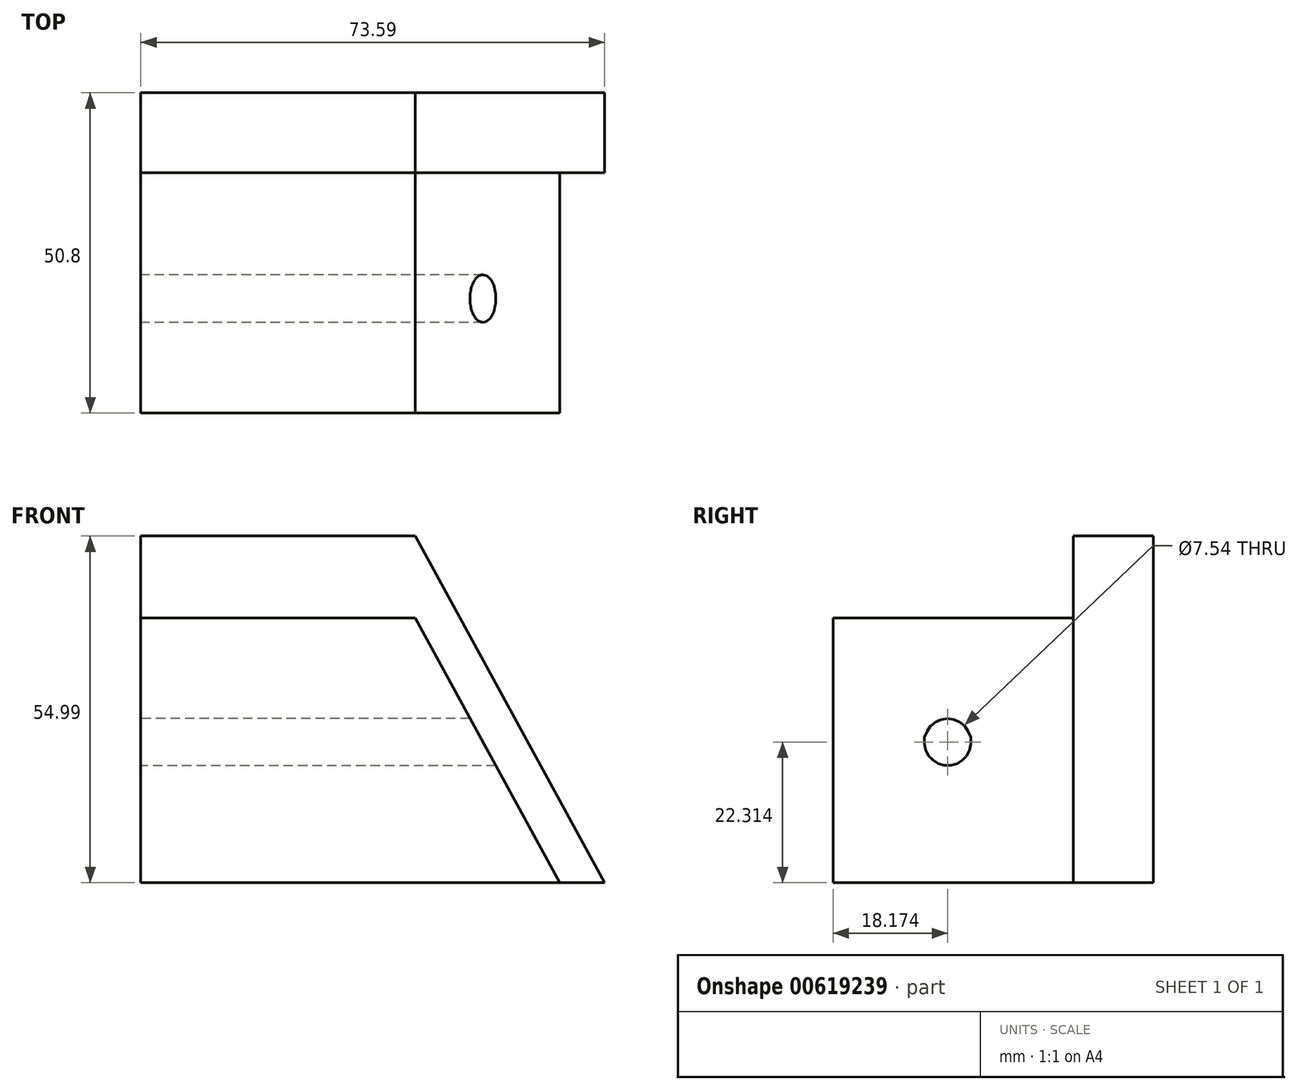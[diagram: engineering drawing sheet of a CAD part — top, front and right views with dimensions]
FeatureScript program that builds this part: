
annotation { "Feature Type Name" : "Feature", "Feature Type Description" : "" }
export const myFeature = defineFeature(function(context is Context, id is Id, definition is map)
    precondition{}
    {
        {
            var Q0;
            Q0=qCreatedBy(makeId("Front.planeOp"),FACE);
            var sketch = newSketch(context, id + "F0", { "sketchPlane" : qUnion([Q0])});
            skLineSegment(sketch, "E0", {"start": v(0, 54.99) * mm, "end": v(43.53, 54.99) * mm});
            skLineSegment(sketch, "E1", {"start": v(43.53, 54.99) * mm, "end": v(73.6, 0) * mm});
            skLineSegment(sketch, "E2", {"start": v(73.6, 0) * mm, "end": v(0, 0) * mm});
            skLineSegment(sketch, "E3", {"start": v(0, 0) * mm, "end": v(0, 54.99) * mm});
            skLineSegment(sketch, "E4", {"start": v(0, 41.98) * mm, "end": v(43.53, 41.98) * mm});
            skLineSegment(sketch, "E5", {"start": v(43.53, 41.98) * mm, "end": v(66.48, 0) * mm});
            skSolve(sketch);
        }
        {
            var Q0;
            {var subQ4=sQuery(id+"F0.wireOp",EDGE,"E4");Q0=makeQuery(id+"F0.imprint","IMPRINT",FACE,{"disambiguationData":[TD([[makeQuery(id+"F0.imprint","IMPRINT",EDGE,{"derivedFrom":subQ4}),-1.0]])]});}
            extrude(context, id + "F1", {"entities" : qUnion([Q0]), "depth" : 50.8 * mm, "offsetDistance" : 25.4 * mm});
        }
        {
            var Q0;
            {var subQ4=sQuery(id+"F0.wireOp",EDGE,"E0");Q0=makeQuery(id+"F0.imprint","IMPRINT",FACE,{"disambiguationData":[TD([[makeQuery(id+"F0.imprint","IMPRINT",EDGE,{"derivedFrom":subQ4}),-1.0]])]});}
            extrude(context, id + "F2", {"entities" : qUnion([Q0]), "operationType" : NewBodyOperationType.ADD, "depth" : 12.7 * mm, "offsetDistance" : 25.4 * mm});
        }
        {
            var Q0;
            {var subQ0=sQuery(id+"F0.wireOp",EDGE,"E3");Q0=makeQuery(id+"F2.boolean.opBoolean","MERGE",FACE,{"derivedFrom":[makeQuery(id+"F1.opExtrude","SWEPT_FACE",FACE,{"disambiguationData":[OSD([subQ0])]}),makeQuery(id+"F2.opExtrude","SWEPT_FACE",FACE,{"disambiguationData":[OSD([subQ0])]})]});}
            var sketch = newSketch(context, id + "F3", { "sketchPlane" : qUnion([Q0])});
            skCircle(sketch, "E6", {"center": v(32.63, 22.31) * mm, "radius": 3.77 * mm});
            skSolve(sketch);
        }
        {
            var Q0;
            Q0=makeQuery(id+"F3.imprint","IMPRINT",FACE,{"disambiguationData":[TD([[makeQuery(id+"F3.imprint","IMPRINT",EDGE,{"derivedFrom":sQuery(id+"F3.wireOp",EDGE,"E6")}),1.0]])]});
            extrude(context, id + "F4", {"entities" : qUnion([Q0]), "operationType" : NewBodyOperationType.REMOVE, "endBound" : BoundingType.SYMMETRIC, "oppositeDirection" : true, "depth" : 254 * mm, "offsetDistance" : 25.4 * mm});
        }
    });
